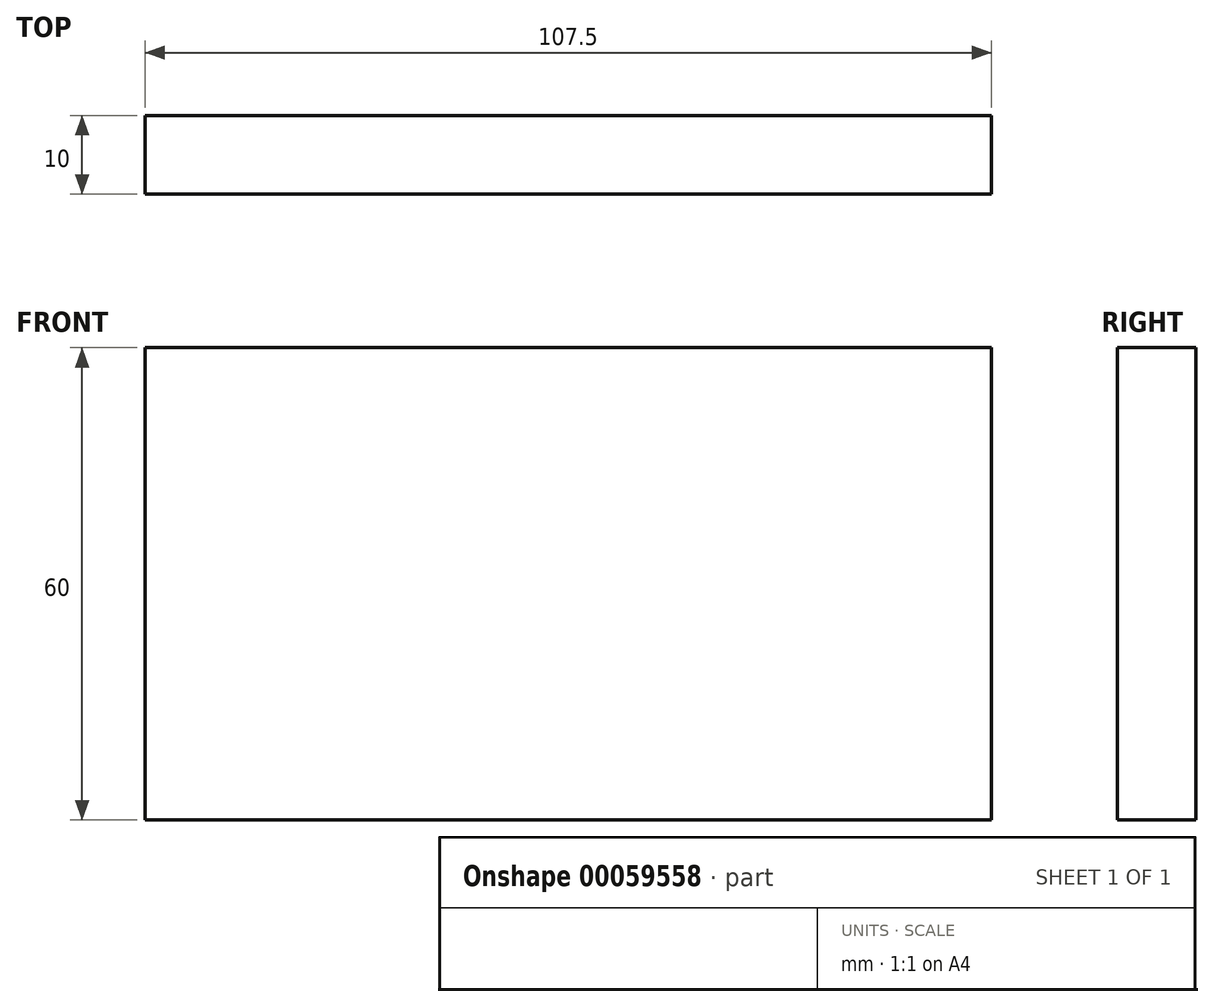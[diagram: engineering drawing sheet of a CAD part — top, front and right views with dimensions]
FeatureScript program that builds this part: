
annotation { "Feature Type Name" : "Feature", "Feature Type Description" : "" }
export const myFeature = defineFeature(function(context is Context, id is Id, definition is map)
    precondition{}
    {
        {
            var Q0;
            Q0=qCreatedBy(makeId("Front.planeOp"),FACE);
            var sketch = newSketch(context, id + "F0", { "sketchPlane" : qUnion([Q0])});
            skLineSegment(sketch, "E0.rect.bottom", {"start": v(-53.75, 30) * mm, "end": v(53.75, 30) * mm});
            skLineSegment(sketch, "E0.rect.top", {"start": v(-53.75, -30) * mm, "end": v(53.75, -30) * mm});
            skLineSegment(sketch, "E0.rect.left", {"start": v(-53.75, 30) * mm, "end": v(-53.75, -30) * mm});
            skLineSegment(sketch, "E0.rect.right", {"start": v(53.75, 30) * mm, "end": v(53.75, -30) * mm});
            skPoint(sketch, "E0.rect.middle", {"position": v(0, 0) * mm});
            skSolve(sketch);
        }
        {
            var Q0;
            Q0=makeQuery(id+"F0.imprint","IMPRINT",FACE,{"disambiguationData":[TD([[makeQuery(id+"F0.imprint","IMPRINT",EDGE,{"derivedFrom":sQuery(id+"F0.wireOp",EDGE,"E0.rect.bottom")}),-1.0]])]});
            extrude(context, id + "F1", {"entities" : qUnion([Q0]), "depth" : 10 * mm});
        }
    });
